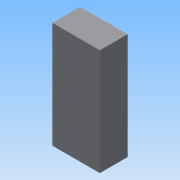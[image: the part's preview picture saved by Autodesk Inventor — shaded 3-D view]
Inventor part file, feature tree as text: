
AUTODESK INVENTOR PART (.ipt)
format: ipt  version: 2015 (Build 190159000, 159)  size: 65,536 bytes
history: native  units: mm
features: extrude x1, sketch x1
ambient origin geometry x8: Origin, YZ Plane, XZ Plane, XY Plane, X Axis, Y Axis, Z Axis, Center Point
bodies: Solid1 (feature_tree)
feature tree (2):
  extrude  "Extrusion1"  [1 undecoded]
  sketch  "Sketch1"  dims[d0=5.0mm d1=0.0mm]
note: 1 required parameter value undecoded (feature->parameter linkage not recoverable at this tier; creation-order binding heuristic only, values carry confidence <= 0.55)
